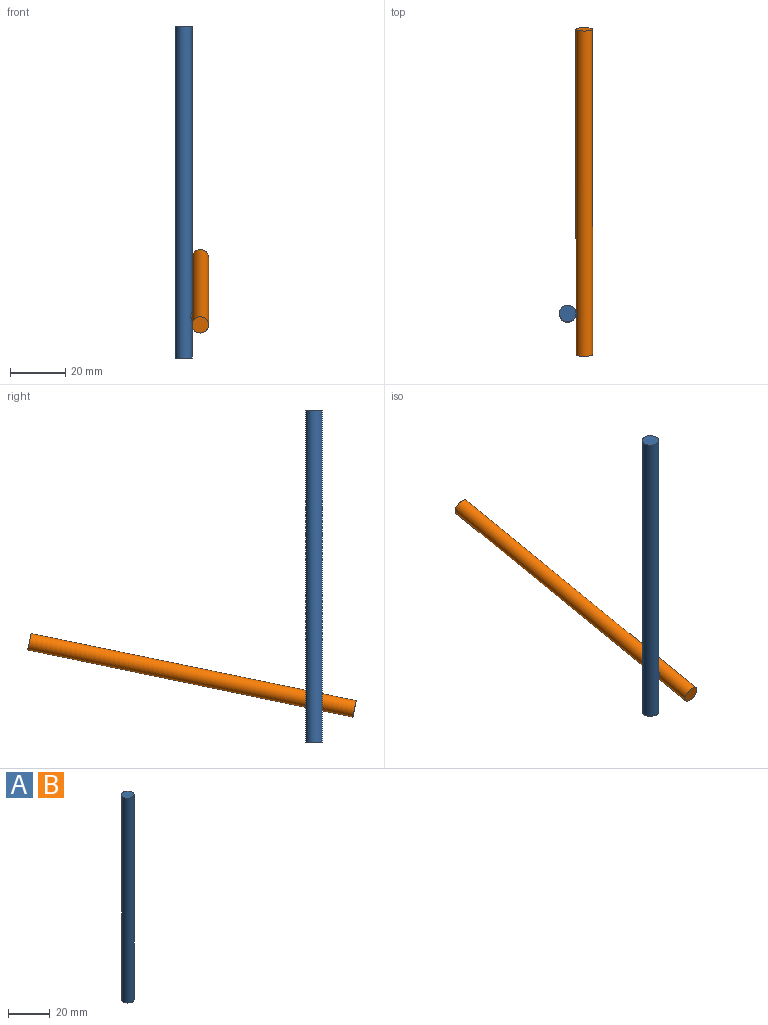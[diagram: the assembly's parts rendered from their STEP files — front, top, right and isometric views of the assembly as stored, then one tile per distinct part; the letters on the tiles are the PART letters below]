
ASSEMBLY  parts=2 mates=1
PART A: 6 faces, bbox 6x6x120 mm
  f0: cylinder r=3mm len=120mm, axis (0,0,1), area 2254.6mm2, adj f1,f2,f3,f5
  f1: plane 6x6mm, normal (0,0,1), area 28.3mm2, adj f0
  f2: plane 6x6mm, normal (0,0,-1), area 28.3mm2, adj f0
  f3: cylinder r=1.5mm len=3mm, axis (1,0,0), area 0.9mm2, adj f0,f4
  f4: plane 3x3mm, normal (1,0,0), area 7.1mm2, adj f3,f5
  f5: cylinder r=1.5mm len=3mm, axis (1,0,0), area 0.9mm2, adj f0,f4
PART B: same geometry as A
PLACE A t=(-19.45,28.71,0.48)mm fixed
PLACE B rot(axis=(0,-0.63,-0.78),180deg) t=(-13.45,14.02,12.45)mm
MATE revolute A.f3 <-> B.f3  axis (1,0,0) through (-16.45,28.71,15.48)mm
